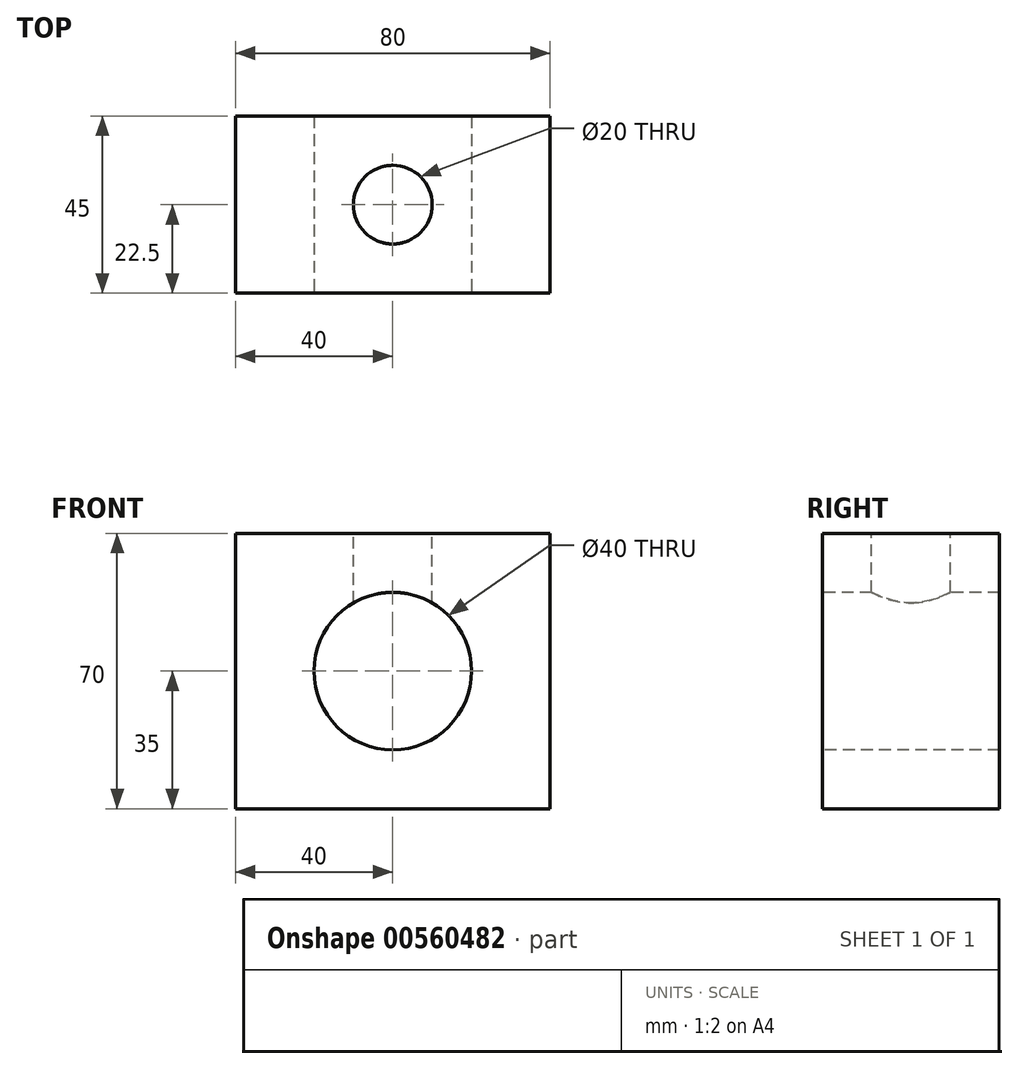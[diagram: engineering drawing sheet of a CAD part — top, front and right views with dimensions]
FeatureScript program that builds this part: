
annotation { "Feature Type Name" : "Feature", "Feature Type Description" : "" }
export const myFeature = defineFeature(function(context is Context, id is Id, definition is map)
    precondition{}
    {
        {
            var Q0;
            Q0=qCreatedBy(makeId("Front.planeOp"),FACE);
            var sketch = newSketch(context, id + "F0", { "sketchPlane" : qUnion([Q0])});
            skLineSegment(sketch, "E0.bottom", {"start": v(40, -35) * mm, "end": v(-40, -35) * mm});
            skLineSegment(sketch, "E0.top", {"start": v(40, 35) * mm, "end": v(-40, 35) * mm});
            skLineSegment(sketch, "E0.left", {"start": v(40, -35) * mm, "end": v(40, 35) * mm});
            skLineSegment(sketch, "E0.right", {"start": v(-40, -35) * mm, "end": v(-40, 35) * mm});
            skPoint(sketch, "E0.middle", {"position": v(0, 0) * mm});
            skSolve(sketch);
        }
        {
            var Q0;
            Q0=makeQuery(id+"F0.imprint","IMPRINT",FACE,{"disambiguationData":[TD([[makeQuery(id+"F0.imprint","IMPRINT",EDGE,{"derivedFrom":sQuery(id+"F0.wireOp",EDGE,"E0.bottom")}),-1.0]])]});
            extrude(context, id + "F1", {"entities" : qUnion([Q0]), "oppositeDirection" : true, "depth" : 45 * mm, "offsetDistance" : 25 * mm});
        }
        {
            var Q0;
            Q0=makeQuery(id+"F1.opExtrude","CAP_FACE",FACE,{"disambiguationData":[OSD([sQuery(id+"F0.wireOp",EDGE,"E0.bottom"),sQuery(id+"F0.wireOp",EDGE,"E0.top"),sQuery(id+"F0.wireOp",EDGE,"E0.left"),sQuery(id+"F0.wireOp",EDGE,"E0.right")])],"isStart":true});
            var sketch = newSketch(context, id + "F2", { "sketchPlane" : qUnion([Q0])});
            skCircle(sketch, "E1", {"center": v(0, 0) * mm, "radius": 20 * mm});
            skSolve(sketch);
        }
        {
            var Q0;
            Q0=makeQuery(id+"F2.imprint","IMPRINT",FACE,{"disambiguationData":[TD([[makeQuery(id+"F2.imprint","IMPRINT",EDGE,{"derivedFrom":sQuery(id+"F2.wireOp",EDGE,"E1")}),1.0]])]});
            extrude(context, id + "F3", {"entities" : qUnion([Q0]), "operationType" : NewBodyOperationType.REMOVE, "endBound" : BoundingType.THROUGH_ALL, "oppositeDirection" : true, "depth" : 25 * mm, "offsetDistance" : 25 * mm});
        }
        {
            var Q0;
            Q0=makeQuery(id+"F1.opExtrude","SWEPT_FACE",FACE,{"disambiguationData":[OSD([sQuery(id+"F0.wireOp",EDGE,"E0.top")])]});
            var sketch = newSketch(context, id + "F4", { "sketchPlane" : qUnion([Q0])});
            skCircle(sketch, "E2", {"center": v(0, 22.5) * mm, "radius": 10 * mm});
            skPoint(sketch, "E2.centerSnap0", {"position": v(-40, 22.5) * mm});
            skSolve(sketch);
        }
        {
            var Q0;
            Q0 = qSketchRegion(id + "F4", true);
            extrude(context, id + "F5", {"entities" : qUnion([Q0]), "operationType" : NewBodyOperationType.REMOVE, "oppositeDirection" : true, "depth" : 25 * mm, "offsetDistance" : 25 * mm});
        }
    });
